# Revit family: Навес Артель Арт 21616
name_source: partatom
category: Антураж
revit_build: Autodesk Revit 2018 (Build: 20180423_1000(x64)
units: mm (PartAtom-declared; Revit-internal decimal feet)

## family parameters
Всегда вертикально = Да
Источник визуального образа = Геометрия семейства
На основе рабочей плоскости = Нет
Общий = Нет
При загрузке вырезать с полостями = Нет
Точка расчета площади = Нет

## types (2) — shared parameters
URL = https://hobbyka.ru
Артикул товара = 21616
Высота = 2500 мм
Группа модели = Навесы и беседки
Изготовитель = ООО «Хоббика»
Изображение типоразмера = Навес «Артель» 21616.jpg
Материал изделия = Сталь, дерево
Цвет каркаса = По умолчанию
Цвет панелей = Дерево
Ширина = 2050 мм

## per-type parameters (varying)
| type | Длина | Кол-во стоек | Модель 3,32 | Модель 5,63 |
| Навес «Артель» Модель 3,32х2,05х2,5 | 3320 мм | 3 | Да | Нет |
| Навес «Артель» Модель 5,63х2,05х2,5 | 5630 мм | 4 | Нет | Да |

note: column(s) folded — value = type name in every type: Описание
